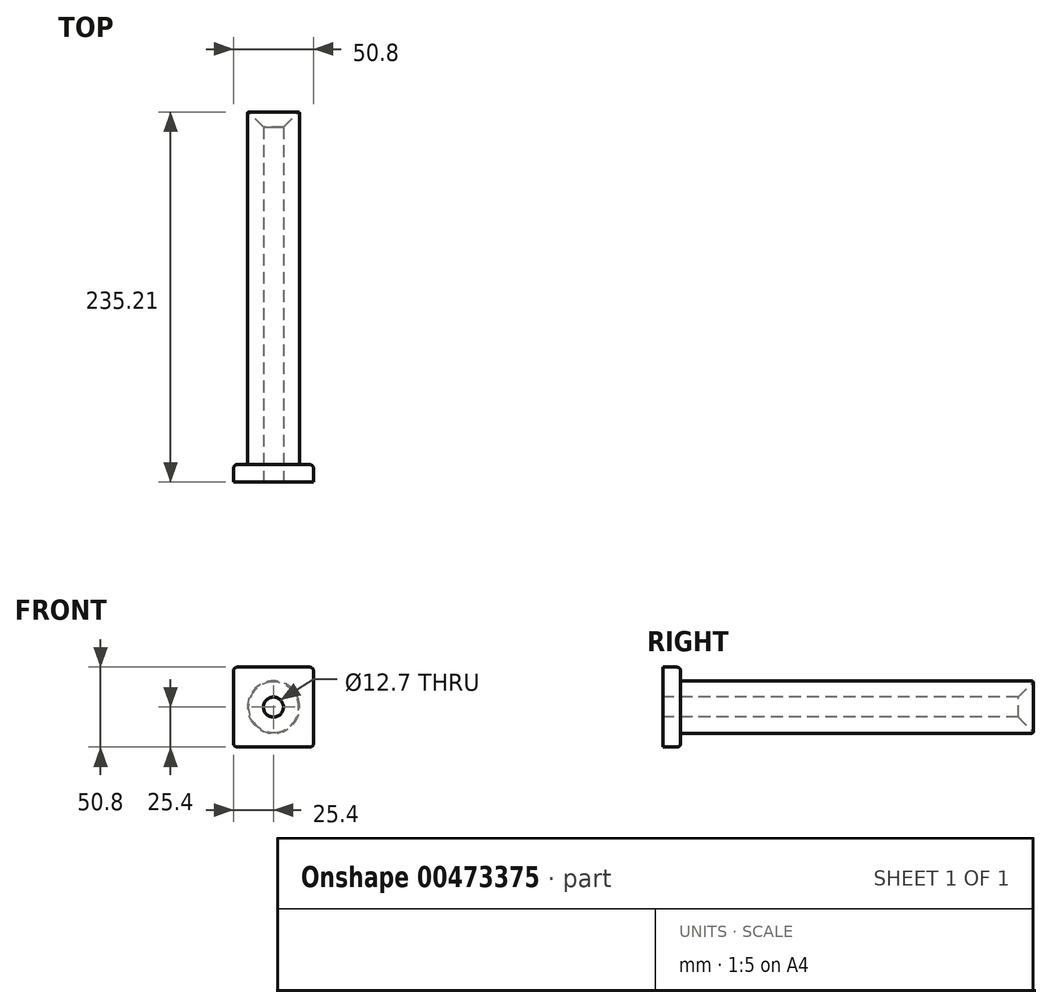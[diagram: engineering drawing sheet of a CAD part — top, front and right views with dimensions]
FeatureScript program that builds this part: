
annotation { "Feature Type Name" : "Feature", "Feature Type Description" : "" }
export const myFeature = defineFeature(function(context is Context, id is Id, definition is map)
    precondition{}
    {
        {
            var Q0;
            Q0=qCreatedBy(makeId("Front.planeOp"),FACE);
            var sketch = newSketch(context, id + "F0", { "sketchPlane" : qUnion([Q0])});
            skLineSegment(sketch, "E0", {"start": v(-25.4, 25.4) * mm, "end": v(-25.4, -25.4) * mm});
            skLineSegment(sketch, "E1", {"start": v(-25.4, -25.4) * mm, "end": v(25.4, -25.4) * mm});
            skLineSegment(sketch, "E2", {"start": v(25.4, -25.4) * mm, "end": v(25.4, 25.4) * mm});
            skLineSegment(sketch, "E3", {"start": v(25.4, 25.4) * mm, "end": v(-25.4, 25.4) * mm});
            skCircle(sketch, "E4", {"center": v(0, 0) * mm, "radius": 25.4 * mm, "construction": true});
            skCircle(sketch, "E5", {"center": v(0, 0) * mm, "radius": 6.35 * mm});
            skCircle(sketch, "E6", {"center": v(0, 0) * mm, "radius": 16.6 * mm});
            skSolve(sketch);
        }
        {
            var Q0;
            Q0=makeQuery(id+"F0.imprint","IMPRINT",FACE,{"disambiguationData":[TD([[makeQuery(id+"F0.imprint","IMPRINT",EDGE,{"derivedFrom":sQuery(id+"F0.wireOp",EDGE,"E0")}),1.0]])]});
            extrude(context, id + "F1", {"entities" : qUnion([Q0]), "oppositeDirection" : true, "depth" : 11.18 * mm});
        }
        {
            var Q0;
            Q0=makeQuery(id+"F0.imprint","IMPRINT",FACE,{"disambiguationData":[TD([[makeQuery(id+"F0.imprint","IMPRINT",EDGE,{"derivedFrom":sQuery(id+"F0.wireOp",EDGE,"E5")}),-1.0]])]});
            extrude(context, id + "F2", {"entities" : qUnion([Q0]), "operationType" : NewBodyOperationType.ADD, "oppositeDirection" : true, "depth" : 235.71 * mm});
        }
        {
            var Q0;
            Q0=makeQuery(id+"F1.opExtrude","CAP_EDGE",EDGE,{"disambiguationData":[OSD([sQuery(id+"F0.wireOp",EDGE,"E0")])],"isStart":false});
            fillet(context, id + "F3", {"entities" : qUnion([Q0]), "radius" : 2.45 * mm, "tangentPropagation" : true, "allowEdgeOverflow" : false});
        }
        {
            var Q0;
            Q0=makeQuery(id+"F1.opExtrude","CAP_EDGE",EDGE,{"disambiguationData":[OSD([sQuery(id+"F0.wireOp",EDGE,"E3")])],"isStart":false});
            fillet(context, id + "F4", {"entities" : qUnion([Q0]), "radius" : 2.45 * mm, "tangentPropagation" : true, "allowEdgeOverflow" : false});
        }
        {
            var Q0;
            Q0=makeQuery(id+"F1.opExtrude","CAP_EDGE",EDGE,{"disambiguationData":[OSD([sQuery(id+"F0.wireOp",EDGE,"E2")])],"isStart":false});
            fillet(context, id + "F5", {"entities" : qUnion([Q0]), "radius" : 2.45 * mm, "tangentPropagation" : true, "allowEdgeOverflow" : false});
        }
        {
            var Q0;
            Q0=makeQuery(id+"F1.opExtrude","CAP_EDGE",EDGE,{"disambiguationData":[OSD([sQuery(id+"F0.wireOp",EDGE,"E1")])],"isStart":false});
            fillet(context, id + "F6", {"entities" : qUnion([Q0]), "radius" : 2.45 * mm, "tangentPropagation" : true, "allowEdgeOverflow" : false});
        }
        {
            var Q0;
            Q0=makeQuery(id+"F2.opExtrude","CAP_EDGE",EDGE,{"disambiguationData":[OSD([sQuery(id+"F0.wireOp",EDGE,"E6")])],"isStart":false});
            fillet(context, id + "F7", {"entities" : qUnion([Q0]), "radius" : 1.84 * mm, "tangentPropagation" : true, "allowEdgeOverflow" : false});
        }
        {
            var Q0;
            Q0=makeQuery(id+"F2.opExtrude","CAP_EDGE",EDGE,{"disambiguationData":[OSD([sQuery(id+"F0.wireOp",EDGE,"E5")])],"isStart":false});
            chamfer(context, id + "F8", {"entities" : qUnion([Q0]), "width" : 10.16 * mm, "tangentPropagation" : true});
        }
    });
